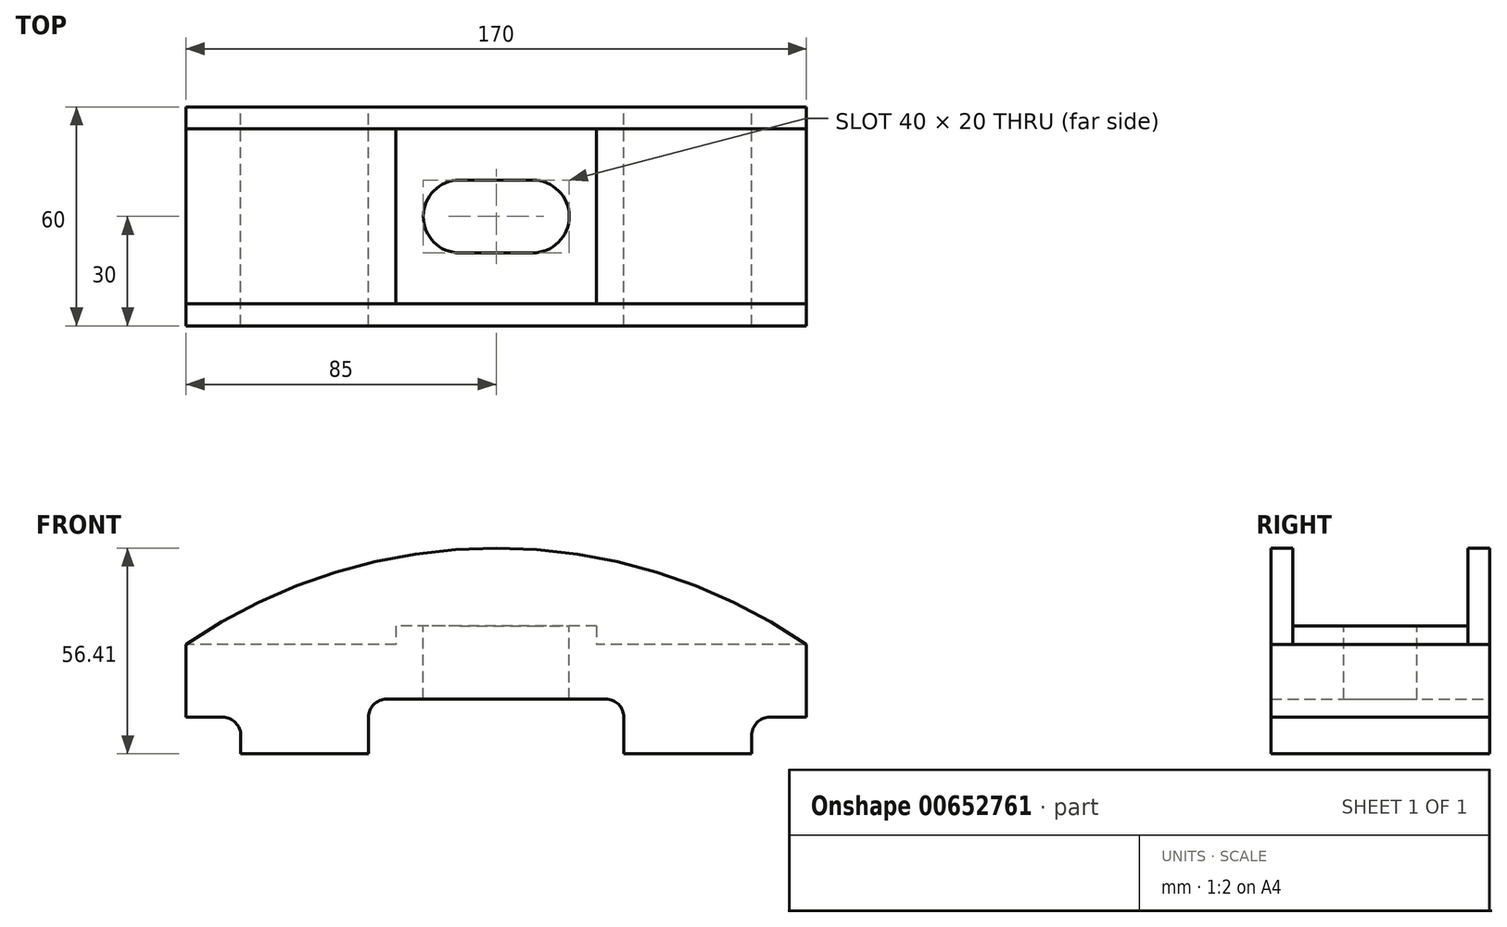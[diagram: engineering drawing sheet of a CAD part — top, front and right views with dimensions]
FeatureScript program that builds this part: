
annotation { "Feature Type Name" : "Feature", "Feature Type Description" : "" }
export const myFeature = defineFeature(function(context is Context, id is Id, definition is map)
    precondition{}
    {
        {
            var Q0;
            Q0=qCreatedBy(makeId("Top.planeOp"),FACE);
            var sketch = newSketch(context, id + "F0", { "sketchPlane" : qUnion([Q0])});
            skLineSegment(sketch, "E0.bottom", {"start": v(85, -30) * mm, "end": v(-85, -30) * mm});
            skLineSegment(sketch, "E0.top", {"start": v(85, 30) * mm, "end": v(-85, 30) * mm});
            skLineSegment(sketch, "E0.left", {"start": v(85, -30) * mm, "end": v(85, 30) * mm});
            skLineSegment(sketch, "E0.right", {"start": v(-85, -30) * mm, "end": v(-85, 30) * mm});
            skPoint(sketch, "E0.middle", {"position": v(0, 0) * mm});
            skSolve(sketch);
        }
        {
            var Q0;
            Q0 = qSketchRegion(id + "F0", true);
            extrude(context, id + "F1", {"entities" : qUnion([Q0]), "depth" : 30 * mm, "offsetDistance" : 25 * mm});
        }
        {
            var Q0;
            Q0=makeQuery(id+"F1.opExtrude","CAP_FACE",FACE,{"disambiguationData":[OSD([sQuery(id+"F0.wireOp",EDGE,"E0.bottom"),sQuery(id+"F0.wireOp",EDGE,"E0.top"),sQuery(id+"F0.wireOp",EDGE,"E0.left"),sQuery(id+"F0.wireOp",EDGE,"E0.right")])],"isStart":false});
            var sketch = newSketch(context, id + "F2", { "sketchPlane" : qUnion([Q0])});
            skLineSegment(sketch, "E1.bottom", {"start": v(10, -10) * mm, "end": v(-10, -10) * mm});
            skLineSegment(sketch, "E1.top", {"start": v(10, 10) * mm, "end": v(-10, 10) * mm});
            skLineSegment(sketch, "E1.left", {"start": v(10, -10) * mm, "end": v(10, 10) * mm});
            skLineSegment(sketch, "E1.right", {"start": v(-10, -10) * mm, "end": v(-10, 10) * mm});
            skPoint(sketch, "E1.middle", {"position": v(0, 0) * mm});
            skCircle(sketch, "E2", {"center": v(10, 0) * mm, "radius": 10 * mm});
            skCircle(sketch, "E3", {"center": v(-10, 0) * mm, "radius": 10 * mm});
            skSolve(sketch);
        }
        {
            var Q0;
            Q0 = qSketchRegion(id + "F2", true);
            extrude(context, id + "F3", {"entities" : qUnion([Q0]), "operationType" : NewBodyOperationType.REMOVE, "endBound" : BoundingType.THROUGH_ALL, "oppositeDirection" : true, "depth" : 25 * mm, "offsetDistance" : 25 * mm});
        }
        {
            var Q0;
            Q0=makeQuery(id+"F1.opExtrude","SWEPT_FACE",FACE,{"disambiguationData":[OSD([sQuery(id+"F0.wireOp",EDGE,"E0.top")])]});
            var sketch = newSketch(context, id + "F4", { "sketchPlane" : qUnion([Q0])});
            skLineSegment(sketch, "E4", {"start": v(0, 0) * mm, "end": v(35, 0) * mm});
            skLineSegment(sketch, "E5", {"start": v(0, 0) * mm, "end": v(-35, 0) * mm});
            skLineSegment(sketch, "E6", {"start": v(-35, 0) * mm, "end": v(-35, 10) * mm});
            skLineSegment(sketch, "E7", {"start": v(35, 0) * mm, "end": v(35, 10) * mm});
            skLineSegment(sketch, "E8", {"start": v(30, 15) * mm, "end": v(-30, 15) * mm});
            skPoint(sketch, "E9.visualSharp", {"position": v(-35, 15) * mm});
            skArc(sketch, "E9.filletArc", {"start": v(-30, 15) * mm, "mid": v(-33.54, 13.54) * mm, "end": v(-35, 10) * mm});
            skPoint(sketch, "E10.visualSharp", {"position": v(35, 15) * mm});
            skArc(sketch, "E10.filletArc", {"start": v(35, 10) * mm, "mid": v(33.54, 13.54) * mm, "end": v(30, 15) * mm});
            skSolve(sketch);
        }
        {
            var Q0;
            Q0 = qSketchRegion(id + "F4", true);
            extrude(context, id + "F5", {"entities" : qUnion([Q0]), "operationType" : NewBodyOperationType.REMOVE, "endBound" : BoundingType.THROUGH_ALL, "oppositeDirection" : true, "depth" : 25 * mm, "offsetDistance" : 25 * mm});
        }
        {
            var Q0;
            Q0=makeQuery(id+"F1.opExtrude","CAP_FACE",FACE,{"disambiguationData":[OSD([sQuery(id+"F0.wireOp",EDGE,"E0.bottom"),sQuery(id+"F0.wireOp",EDGE,"E0.top"),sQuery(id+"F0.wireOp",EDGE,"E0.left"),sQuery(id+"F0.wireOp",EDGE,"E0.right")])],"isStart":false});
            var sketch = newSketch(context, id + "F6", { "sketchPlane" : qUnion([Q0])});
            skLineSegment(sketch, "E11.bottom", {"start": v(27.5, -24) * mm, "end": v(-27.5, -24) * mm});
            skLineSegment(sketch, "E11.top", {"start": v(27.5, 24) * mm, "end": v(-27.5, 24) * mm});
            skLineSegment(sketch, "E11.left", {"start": v(27.5, -24) * mm, "end": v(27.5, 24) * mm});
            skLineSegment(sketch, "E11.right", {"start": v(-27.5, -24) * mm, "end": v(-27.5, 24) * mm});
            skPoint(sketch, "E11.middle", {"position": v(0, 0) * mm});
            skSolve(sketch);
        }
        {
            var Q0;
            Q0 = qSketchRegion(id + "F6", true);
            extrude(context, id + "F7", {"entities" : qUnion([Q0]), "operationType" : NewBodyOperationType.ADD, "depth" : 5 * mm, "offsetDistance" : 25 * mm});
        }
        {
            var Q0;
            Q0=makeQuery(id+"F7.opExtrude","CAP_FACE",FACE,{"disambiguationData":[OSD([sQuery(id+"F6.wireOp",EDGE,"E11.bottom"),sQuery(id+"F6.wireOp",EDGE,"E11.top"),sQuery(id+"F6.wireOp",EDGE,"E11.left"),sQuery(id+"F6.wireOp",EDGE,"E11.right")])],"isStart":true});
            extrude(context, id + "F8", {"entities" : qUnion([Q0]), "operationType" : NewBodyOperationType.REMOVE, "oppositeDirection" : true, "depth" : 25 * mm, "offsetDistance" : 25 * mm});
        }
        {
            var Q0;
            Q0=makeQuery(id+"F1.opExtrude","SWEPT_FACE",FACE,{"disambiguationData":[OSD([sQuery(id+"F0.wireOp",EDGE,"E0.top")])]});
            var sketch = newSketch(context, id + "F9", { "sketchPlane" : qUnion([Q0])});
            skLineSegment(sketch, "E12", {"start": v(-85, 0) * mm, "end": v(-85, 10) * mm});
            skLineSegment(sketch, "E13", {"start": v(-85, 10) * mm, "end": v(-75, 10) * mm});
            skLineSegment(sketch, "E14", {"start": v(-70, 5) * mm, "end": v(-70, 0) * mm});
            skLineSegment(sketch, "E15", {"start": v(85, 0) * mm, "end": v(70, 0) * mm});
            skLineSegment(sketch, "E16", {"start": v(75, 10) * mm, "end": v(85, 10) * mm});
            skLineSegment(sketch, "E17", {"start": v(70, 5) * mm, "end": v(70, 0) * mm});
            skPoint(sketch, "E18.visualSharp", {"position": v(-70, 10) * mm});
            skArc(sketch, "E18.filletArc", {"start": v(-70, 5) * mm, "mid": v(-71.46, 8.54) * mm, "end": v(-75, 10) * mm});
            skPoint(sketch, "E19.visualSharp", {"position": v(70, 10) * mm});
            skArc(sketch, "E19.filletArc", {"start": v(75, 10) * mm, "mid": v(71.46, 8.54) * mm, "end": v(70, 5) * mm});
            skSolve(sketch);
        }
        {
            var Q0;
            {var subQ0=sQuery(id+"F9.wireOp",EDGE,"E15");Q0=makeQuery(id+"F9.imprint","IMPRINT",FACE,{"disambiguationData":[TD([[makeQuery(id+"F9.imprint","IMPRINT",EDGE,{"derivedFrom":subQ0}),1.0]])]});}
            var Q1;
            {var subQ1=sQuery(id+"F9.wireOp",EDGE,"E12");Q1=makeQuery(id+"F9.imprint","IMPRINT",FACE,{"disambiguationData":[TD([[makeQuery(id+"F9.imprint","IMPRINT",EDGE,{"derivedFrom":subQ1}),1.0]])]});}
            extrude(context, id + "F10", {"entities" : qUnion([Q0, Q1]), "operationType" : NewBodyOperationType.REMOVE, "endBound" : BoundingType.THROUGH_ALL, "oppositeDirection" : true, "depth" : 25 * mm, "offsetDistance" : 25 * mm});
        }
        {
            var Q0;
            Q0=makeQuery(id+"F1.opExtrude","SWEPT_FACE",FACE,{"disambiguationData":[OSD([sQuery(id+"F0.wireOp",EDGE,"E0.top")])]});
            var sketch = newSketch(context, id + "F11", { "sketchPlane" : qUnion([Q0])});
            skArc(sketch, "E20", {"start": v(85, 30) * mm, "mid": v(0, 56.4) * mm, "end": v(-85, 30) * mm});
            skSolve(sketch);
        }
        {
            var Q0;
            Q0=makeQuery(id+"F1.opExtrude","SWEPT_FACE",FACE,{"disambiguationData":[OSD([sQuery(id+"F0.wireOp",EDGE,"E0.bottom")])]});
            var sketch = newSketch(context, id + "F12", { "sketchPlane" : qUnion([Q0])});
            skArc(sketch, "E21", {"start": v(85, 30) * mm, "mid": v(0, 56.4) * mm, "end": v(-85, 30) * mm});
            skSolve(sketch);
        }
        {
            var Q0;
            Q0=makeQuery(id+"F12.imprint","IMPRINT",FACE,{"disambiguationData":[TD([[makeQuery(id+"F12.imprint","IMPRINT",EDGE,{"derivedFrom":sQuery(id+"F12.wireOp",EDGE,"E21")}),1.0]])]});
            extrude(context, id + "F13", {"entities" : qUnion([Q0]), "operationType" : NewBodyOperationType.ADD, "oppositeDirection" : true, "depth" : 6 * mm, "offsetDistance" : 25 * mm});
        }
        {
            var Q0;
            Q0=makeQuery(id+"F11.imprint","IMPRINT",FACE,{"disambiguationData":[TD([[makeQuery(id+"F11.imprint","IMPRINT",EDGE,{"derivedFrom":sQuery(id+"F11.wireOp",EDGE,"E20")}),1.0]])]});
            extrude(context, id + "F14", {"entities" : qUnion([Q0]), "oppositeDirection" : true, "depth" : 6 * mm, "offsetDistance" : 25 * mm});
        }
        {
            var Q0;
            Q0=makeQuery(id+"F14.opExtrude","SWEPT_BODY",BODY,{"disambiguationData":[OSD([sQuery(id+"F0.wireOp",EDGE,"E0.top"),sQuery(id+"F11.wireOp",EDGE,"E20")])]});
            deleteBodies(context, id + "F15", {"entities" : qUnion([Q0])});
        }
        {
            var Q0;
            Q0=makeQuery(id+"F1.opExtrude","SWEPT_FACE",FACE,{"disambiguationData":[OSD([sQuery(id+"F0.wireOp",EDGE,"E0.top")])]});
            var sketch = newSketch(context, id + "F16", { "sketchPlane" : qUnion([Q0])});
            skArc(sketch, "E22", {"start": v(85, 30) * mm, "mid": v(0, 56.4) * mm, "end": v(-85, 30) * mm});
            skSolve(sketch);
        }
        {
            var Q0;
            Q0=makeQuery(id+"F16.imprint","IMPRINT",FACE,{"disambiguationData":[TD([[makeQuery(id+"F16.imprint","IMPRINT",EDGE,{"derivedFrom":sQuery(id+"F16.wireOp",EDGE,"E22")}),1.0]])]});
            extrude(context, id + "F17", {"entities" : qUnion([Q0]), "operationType" : NewBodyOperationType.ADD, "oppositeDirection" : true, "depth" : 6 * mm, "offsetDistance" : 25 * mm});
        }
    });
